# Revit family: НЕВАТОМ_Вентилятор VKPN, версия 1
name_source: partatom
category: Оборудование
revit_build: Autodesk Revit 2017 (Build: 20170118_1100(x64)
units: mm (PartAtom-declared; Revit-internal decimal feet)

## family parameters
Всегда вертикально = Да
На основе рабочей плоскости = Нет
Общий = Нет
При загрузке вырезать с полостями = Нет
Размер круглого соединителя = Использовать диаметр
Тип детали = Вставляется
Точка расчета площади = Нет

## types (11) — shared parameters
ADSK_Единица измерения = шт.
ADSK_Завод-изготовитель = НЕВАТОМ
ADSK_Количество = 1
ADSK_Материал наименование = Оцинкованная сталь
ADSK_Наименование = Вентилятор канальный прямоугольный с назад загнутыми лопатками
Nevatom_URL = https://t.me
Ключевая пометка = Вентиляция
Крышка = СВМПЭ, белый
Материал = Сталь серая

## per-type parameters (varying)
| type | 1 | 2 | A | ADSK_Масса | ADSK_Масса_Текст | ADSK_Напряжение | ADSK_Полная мощность | ADSK_Размер_Высота | ADSK_Размер_Длина | ADSK_Размер_Ширина | ADSK_Расход воздуха | ADSK_Ток | ADSK_Частота вращения вентилятора | B | E | F | H | L | Полное давление |
| VKPN 400-200/22-2E | 260 мм | 60 мм | 400 мм | 9.3 | 9.3 кг | 230 В | 0 кВт | 265 мм | 440 мм | 450 мм | 1100.0 м³/ч | 1 А | 2600 | 200 мм | 440 мм | 240 мм | 265 мм | 450 мм | 480.0 Па |
| VKPN 800-500/50-4D | 520 мм | 120 мм | 800 мм | 60.3 | 60.3 кг | 380 В | 2 кВт | 575 мм | 860 мм | 815 мм | 7400.0 м³/ч | 3 А | 1330 | 500 мм | 860 мм | 560 мм | 575 мм | 815 мм | 510.0 Па |
| VKPN 500-250/25-2E | 325 мм | 75 мм | 500 мм | 14.3 | 14.3 кг | 230 В | 0 кВт | 315 мм | 540 мм | 490 мм | 1400.0 м³/ч | 1 А | 2600 | 250 мм | 540 мм | 290 мм | 315 мм | 490 мм | 650.0 Па |
| VKPN 500-300/28-2E | 325 мм | 75 мм | 500 мм | 15.6 | 15.6 кг | 230 В | 0 кВт | 365 мм | 540 мм | 500 мм | 1800.0 м³/ч | 1 А | 2500 | 300 мм | 540 мм | 340 мм | 365 мм | 500 мм | 600.0 Па |
| VKPN 600-300/35-4E | 390 мм | 90 мм | 600 мм | 21.7 | 21.7 кг | 230 В | 0 кВт | 365 мм | 640 мм | 640 мм | 2200.0 м³/ч | 1 А | 1360 | 300 мм | 640 мм | 340 мм | 365 мм | 640 мм | 260.0 Па |
| VKPN 600-300/35-4D | 390 мм | 90 мм | 600 мм | 21.4 | 21.4 кг | 380 В | 0 кВт | 415 мм | 640 мм | 640 мм | 2500.0 м³/ч | 0 А | 2200 | 300 мм | 640 мм | 340 мм | 415 мм | 640 мм | 300.0 Па |
| VKPN 600-350/40-4E | 390 мм | 90 мм | 600 мм | 28.2 | 28.2 кг | 230 В | 1 кВт | 415 мм | 640 мм | 705 мм | 4000.0 м³/ч | 2 А | 1350 | 350 мм | 640 мм | 390 мм | 415 мм | 705 мм | 400.0 Па |
| VKPN 600-350/40-4D | 390 мм | 90 мм | 600 мм | 24.8 | 24.8 кг | 380 В | 1 кВт | 475 мм | 640 мм | 705 мм | 4000.0 м³/ч | 1 А | 1350 | 350 мм | 640 мм | 390 мм | 475 мм | 705 мм | 400.0 Па |
| VKPN 700-400/45-4E | 455 мм | 105 мм | 700 мм | 42.8 | 42.8 кг | 230 В | 1 кВт | 475 мм | 740 мм | 787 мм | 5600.0 м³/ч | 4 А | 1340 | 400 мм | 740 мм | 440 мм | 475 мм | 787 мм | 450.0 Па |
| VKPN 700-400/45-4D | 455 мм | 105 мм | 700 мм | 44.6 | 44.6 кг | 380 В | 1 кВт | 475 мм | 740 мм | 787 мм | 5700.0 м³/ч | 1 А | 1280 | 400 мм | 740 мм | 440 мм | 475 мм | 787 мм | 450.0 Па |
| VKPN 900-500/56-4D | 585 мм | 135 мм | 900 мм | 77.4 | 77.4 кг | 380 В | 2 кВт | 575 мм | 960 мм | 915 мм | 10000.0 м³/ч | 4 А | 1325 | 500 мм | 960 мм | 560 мм | 575 мм | 915 мм | 680.0 Па |

note: column(s) folded — value = type name in every type: ADSK_Марка
